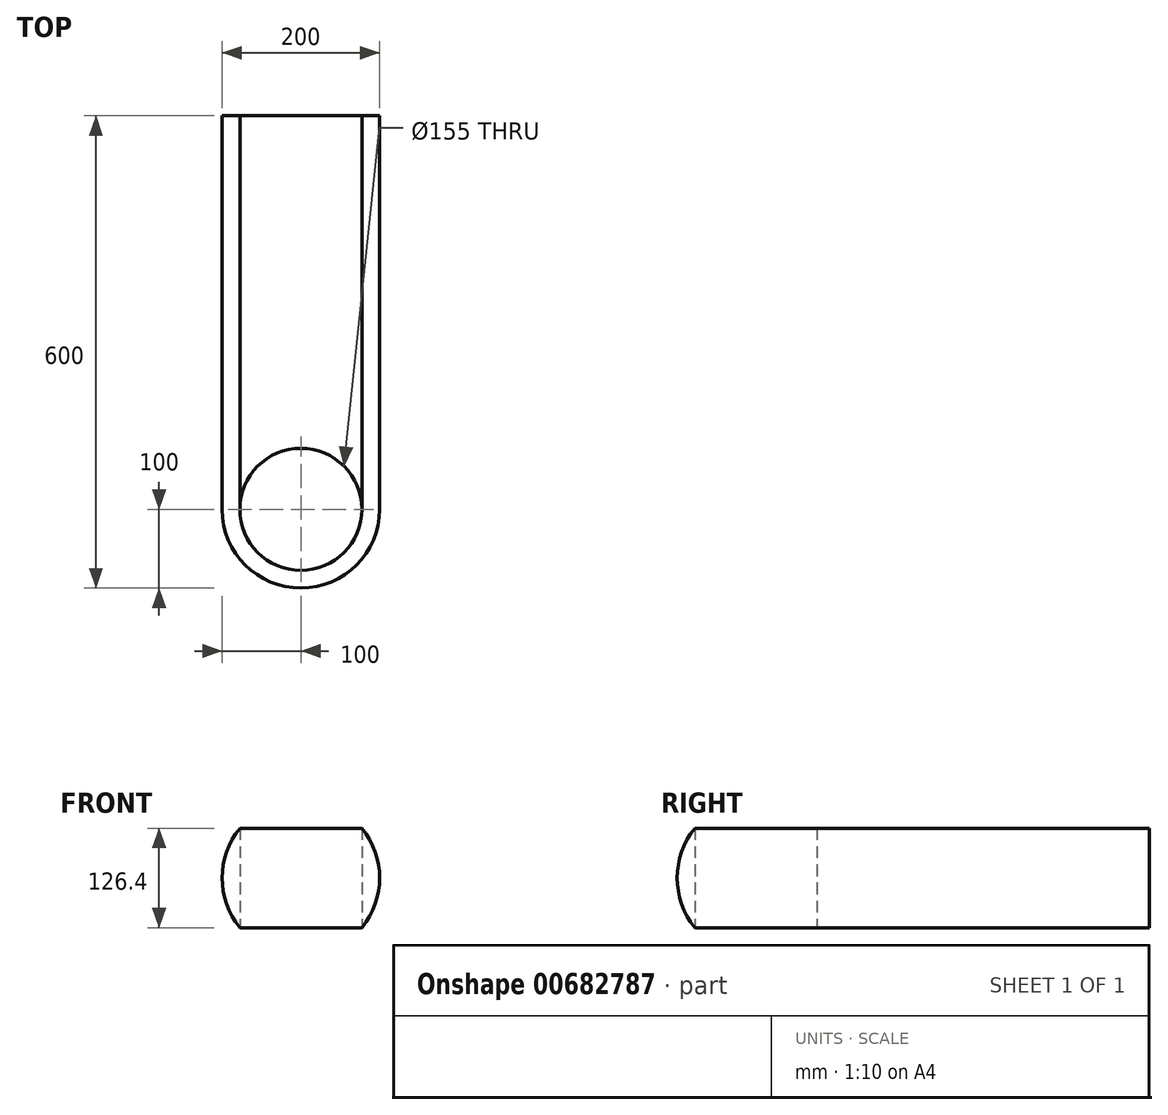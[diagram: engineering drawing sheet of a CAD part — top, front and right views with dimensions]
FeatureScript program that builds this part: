
annotation { "Feature Type Name" : "Feature", "Feature Type Description" : "" }
export const myFeature = defineFeature(function(context is Context, id is Id, definition is map)
    precondition{}
    {
        {
            var Q0;
            Q0=qCreatedBy(makeId("Front.planeOp"),FACE);
            var sketch = newSketch(context, id + "F0", { "sketchPlane" : qUnion([Q0])});
            skArc(sketch, "E0", {"start": v(0, 200) * mm, "mid": v(-100, 100) * mm, "end": v(0, 0) * mm});
            skLineSegment(sketch, "E1", {"start": v(0, 200) * mm, "end": v(0, 0) * mm});
            skSolve(sketch);
        }
        {
            var Q0;
            Q0=makeQuery(id+"F0.imprint","IMPRINT",FACE,{"disambiguationData":[TD([[makeQuery(id+"F0.imprint","IMPRINT",EDGE,{"derivedFrom":sQuery(id+"F0.wireOp",EDGE,"E0")}),1.0]])]});
            var Q1;
            Q1=sQuery(id+"F0.wireOp",EDGE,"E1");
            revolve(context, id + "F1", {"entities" : qUnion([Q0]), "axis" : qUnion([Q1]), "revolveType" : RevolveType.FULL});
        }
        {
            var Q0;
            Q0=qCreatedBy(makeId("Top.planeOp"),FACE);
            cPlane(context, id + "F2", {"entities" : qUnion([Q0]), "cplaneType" : CPlaneType.OFFSET, "offset" : 25 * mm, "oppositeDirection" : true, "width" : 150 * mm, "height" : 150 * mm});
        }
        {
            var Q0;
            Q0=qCreatedBy(id+"F2.planeOp",FACE);
            var sketch = newSketch(context, id + "F3", { "sketchPlane" : qUnion([Q0])});
            skCircle(sketch, "E2", {"center": v(0, 0) * mm, "radius": 77.5 * mm});
            skSolve(sketch);
        }
        {
            var Q0;
            Q0 = qSketchRegion(id + "F3", true);
            extrude(context, id + "F4", {"entities" : qUnion([Q0]), "operationType" : NewBodyOperationType.REMOVE, "endBound" : BoundingType.THROUGH_ALL, "depth" : 25 * mm, "offsetDistance" : 25 * mm});
        }
        {
            var Q0;
            Q0=makeQuery(id+"F4.boolean.opBoolean","COPY",FACE,{"derivedFrom":makeQuery(id+"F4.opExtrude","SWEPT_FACE",FACE,{"disambiguationData":[OSD([sQuery(id+"F3.wireOp",EDGE,"E2")])]})});
            cPlane(context, id + "F5", {"entities" : qUnion([Q0]), "cplaneType" : CPlaneType.LINE_ANGLE, "offset" : 25 * mm, "angle" : 90 * degree, "width" : 150 * mm, "height" : 150 * mm});
        }
        {
            var Q0;
            Q0=qCreatedBy(id+"F5.planeOp",FACE);
            var sketch = newSketch(context, id + "F6", { "sketchPlane" : qUnion([Q0])});
            skLineSegment(sketch, "E3.0", {"start": v(77.5, 163.2) * mm, "end": v(-77.5, 163.2) * mm});
            skLineSegment(sketch, "E4.0", {"start": v(-77.5, 36.8) * mm, "end": v(77.5, 36.8) * mm});
            skLineSegment(sketch, "E5", {"start": v(0, 163.2) * mm, "end": v(0, 36.8) * mm});
            skArc(sketch, "E6", {"start": v(-77.5, 163.2) * mm, "mid": v(-100, 100) * mm, "end": v(-77.5, 36.8) * mm});
            skArc(sketch, "E7.trimOffspring", {"start": v(77.5, 36.8) * mm, "mid": v(100, 100) * mm, "end": v(77.5, 163.2) * mm});
            skSolve(sketch);
        }
        {
            var Q0;
            Q0 = qSketchRegion(id + "F6", true);
            extrude(context, id + "F7", {"entities" : qUnion([Q0]), "operationType" : NewBodyOperationType.ADD, "depth" : 500 * mm, "offsetDistance" : 25 * mm});
        }
        {
            var Q0;
            Q0=qCreatedBy(makeId("Top.planeOp"),FACE);
            var sketch = newSketch(context, id + "F8", { "sketchPlane" : qUnion([Q0])});
            skCircle(sketch, "E8", {"center": v(0, 0) * mm, "radius": 77.5 * mm});
            skSolve(sketch);
        }
        {
            var Q0;
            Q0 = qSketchRegion(id + "F8", true);
            extrude(context, id + "F9", {"entities" : qUnion([Q0]), "operationType" : NewBodyOperationType.REMOVE, "endBound" : BoundingType.THROUGH_ALL, "depth" : 25 * mm, "offsetDistance" : 25 * mm});
        }
    });
